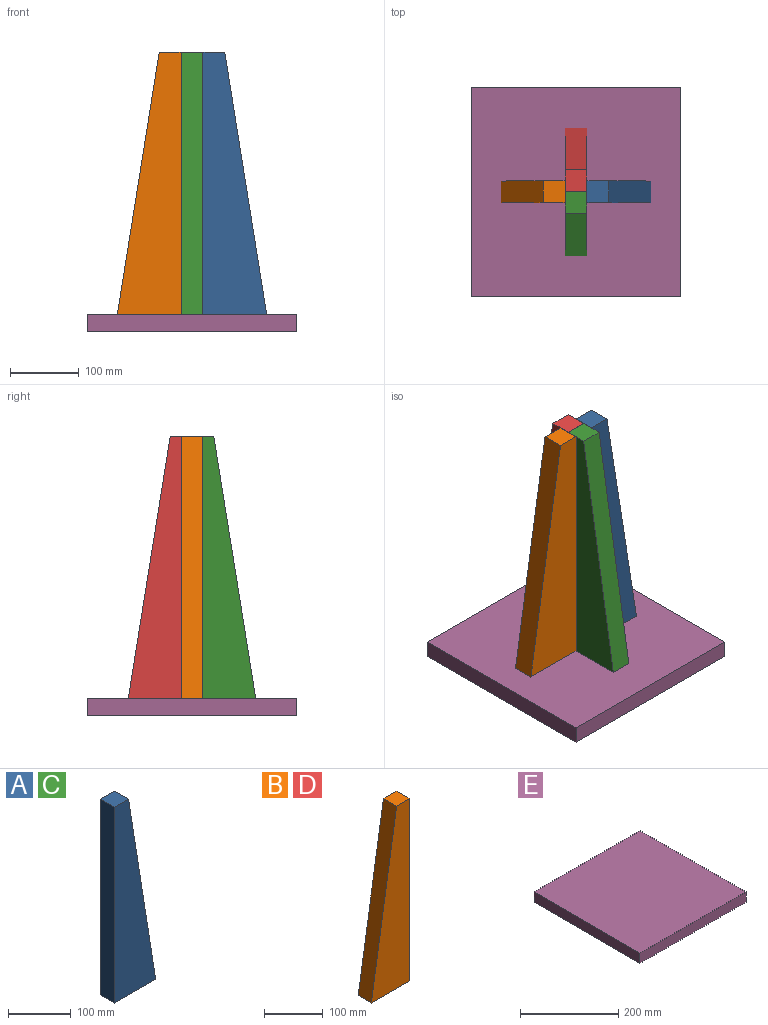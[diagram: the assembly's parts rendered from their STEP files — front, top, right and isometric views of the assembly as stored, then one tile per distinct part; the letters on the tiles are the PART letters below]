
ASSEMBLY  parts=5 mates=3
PART A: 6 faces, bbox 92.7x31.8x381 mm
  f0: plane 92.59x31.75mm, normal (0,0,-1), area 2939.7mm2, adj f1,f3,f4,f5
  f1: plane 381x60.96mm, normal (0.99,0,0.16), area 12250.6mm2, adj f0,f2,f4,f5
  f2: plane 31.78x31.75mm, normal (0,0,1), area 1009mm2, adj f1,f3,f4,f5
  f3: plane 381x31.75mm, normal (-1,0,0), area 12096.7mm2, adj f0,f2,f4,f5
  f4: plane 381x92.74mm, normal (0,-1,0), area 23692.6mm2, adj f0,f1,f2,f3
  f5: plane 381x92.74mm, normal (0,1,0), area 23692.6mm2, adj f0,f1,f2,f3
PART B: 6 faces, bbox 92.7x31.8x381 mm
  f0: plane 381x60.96mm, normal (-0.99,0,0.16), area 12250.6mm2, adj f1,f3,f4,f5
  f1: plane 92.59x31.75mm, normal (0,0,-1), area 2939.7mm2, adj f0,f2,f4,f5
  f2: plane 381x31.75mm, normal (1,0,0), area 12096.7mm2, adj f1,f3,f4,f5
  f3: plane 31.78x31.75mm, normal (0,0,1), area 1009mm2, adj f0,f2,f4,f5
  f4: plane 381x92.74mm, normal (0,-1,0), area 23692.6mm2, adj f0,f1,f2,f3
  f5: plane 381x92.74mm, normal (0,1,0), area 23692.6mm2, adj f0,f1,f2,f3
PART C: same geometry as A
PART D: same geometry as B
PART E: 6 faces, bbox 304.8x304.8x25.4 mm
  f0: plane 304.8x25.4mm, normal (1,0,0), area 7741.9mm2, adj f1,f3,f4,f5
  f1: plane 304.8x25.4mm, normal (0,1,0), area 7741.9mm2, adj f0,f2,f4,f5
  f2: plane 304.8x25.4mm, normal (-1,0,0), area 7741.9mm2, adj f1,f3,f4,f5
  f3: plane 304.8x25.4mm, normal (0,-1,0), area 7741.9mm2, adj f0,f2,f4,f5
  f4: plane 304.8x304.8mm, normal (0,0,1), area 92903mm2, adj f0,f1,f2,f3
  f5: plane 304.8x304.8mm, normal (0,0,-1), area 92903mm2, adj f0,f1,f2,f3
PLACE A rot(axis=(0,1,0),0deg) t=(26.21,36,-274.07)mm
PLACE B rot(axis=(0,-1,0),0deg) t=(-5.52,36,-274.07)mm
PLACE C rot(axis=(0,0,-1),90deg) t=(26.07,19.98,-274.07)mm
PLACE D rot(axis=(0,0,-1),90deg) t=(26.07,19.98,-274.07)mm
PLACE E t=(10.19,20.13,-274.07)mm
MATE fastened D.f1 <-> E.f4  axis (0,0,-1) through (10.19,20.13,-248.67)mm
MATE fastened A.f3 <-> D.f5  axis (-1,0,0) through (26.07,20.13,-248.67)mm
MATE fastened B.f2 <-> D.f4  axis (1,0,0) through (-5.68,20.13,-248.67)mm
